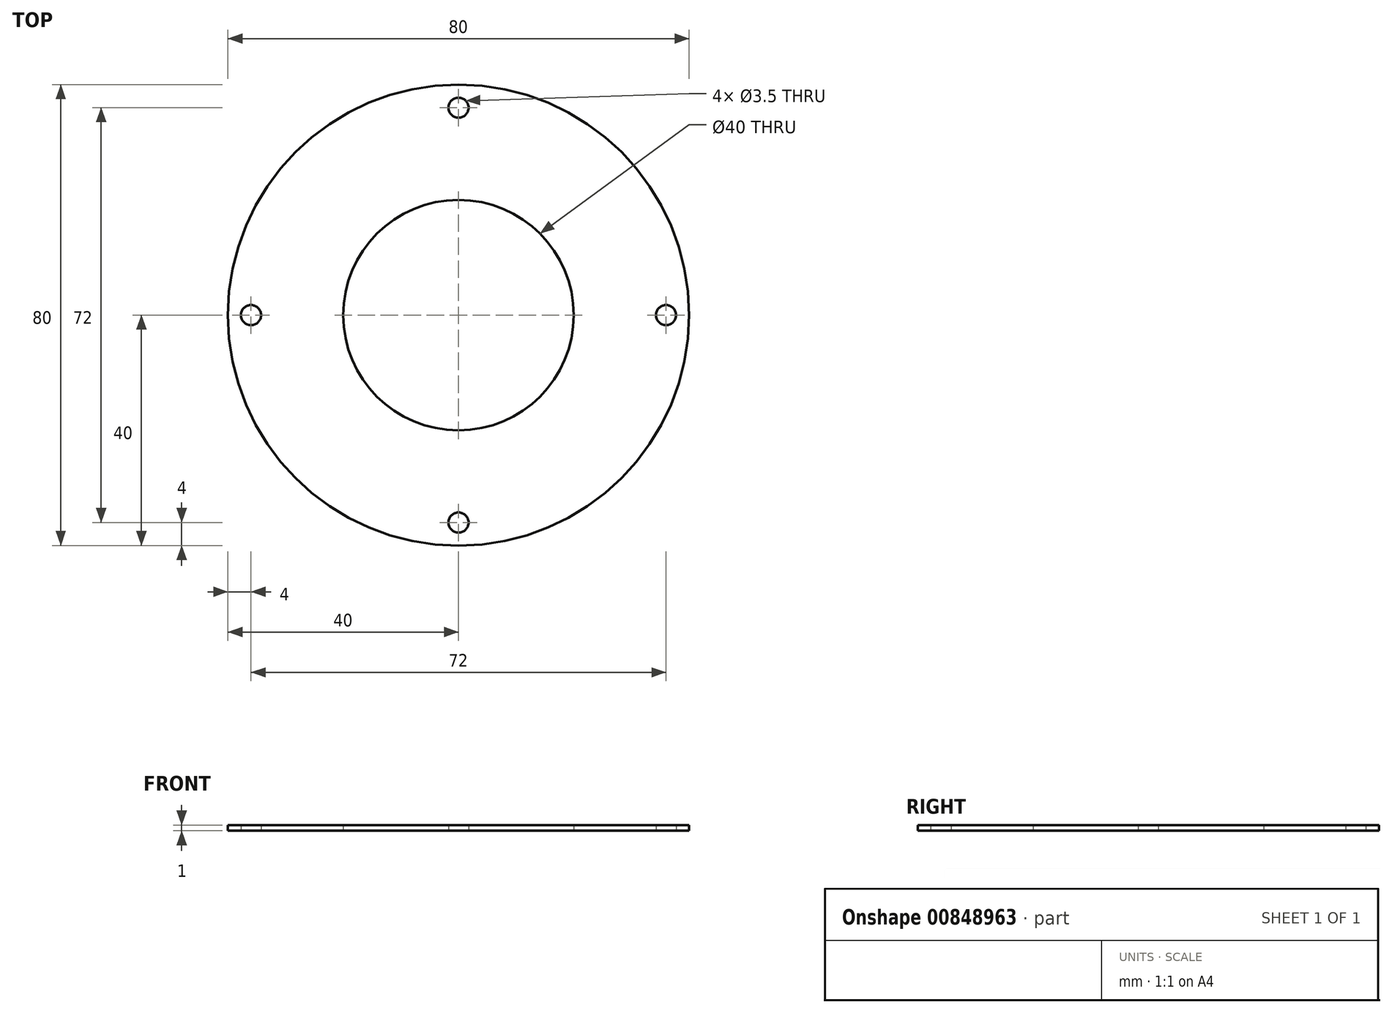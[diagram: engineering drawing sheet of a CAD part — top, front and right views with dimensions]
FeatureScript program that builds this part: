
annotation { "Feature Type Name" : "Feature", "Feature Type Description" : "" }
export const myFeature = defineFeature(function(context is Context, id is Id, definition is map)
    precondition{}
    {
        {
            var Q0;
            Q0=qCreatedBy(makeId("Top.planeOp"),FACE);
            var sketch = newSketch(context, id + "F0", { "sketchPlane" : qUnion([Q0])});
            skCircle(sketch, "E0", {"center": v(0, 0) * mm, "radius": 20 * mm});
            skCircle(sketch, "E1", {"center": v(0, 0) * mm, "radius": 40 * mm});
            skCircle(sketch, "E2", {"center": v(0, 36) * mm, "radius": 1.75 * mm});
            skCircle(sketch, "E3.1.0", {"center": v(36, 0) * mm, "radius": 1.75 * mm});
            skCircle(sketch, "E3.2.0", {"center": v(0, -36) * mm, "radius": 1.75 * mm});
            skCircle(sketch, "E3.3.0", {"center": v(-36, 0) * mm, "radius": 1.75 * mm});
            skSolve(sketch);
        }
        {
            var Q0;
            Q0=makeQuery(id+"F0.imprint","IMPRINT",FACE,{"disambiguationData":[TD([[makeQuery(id+"F0.imprint","IMPRINT",EDGE,{"derivedFrom":sQuery(id+"F0.wireOp",EDGE,"E0")}),-1.0]])]});
            extrude(context, id + "F1", {"entities" : qUnion([Q0]), "depth" : 1 * mm, "offsetDistance" : 25 * mm});
        }
    });
